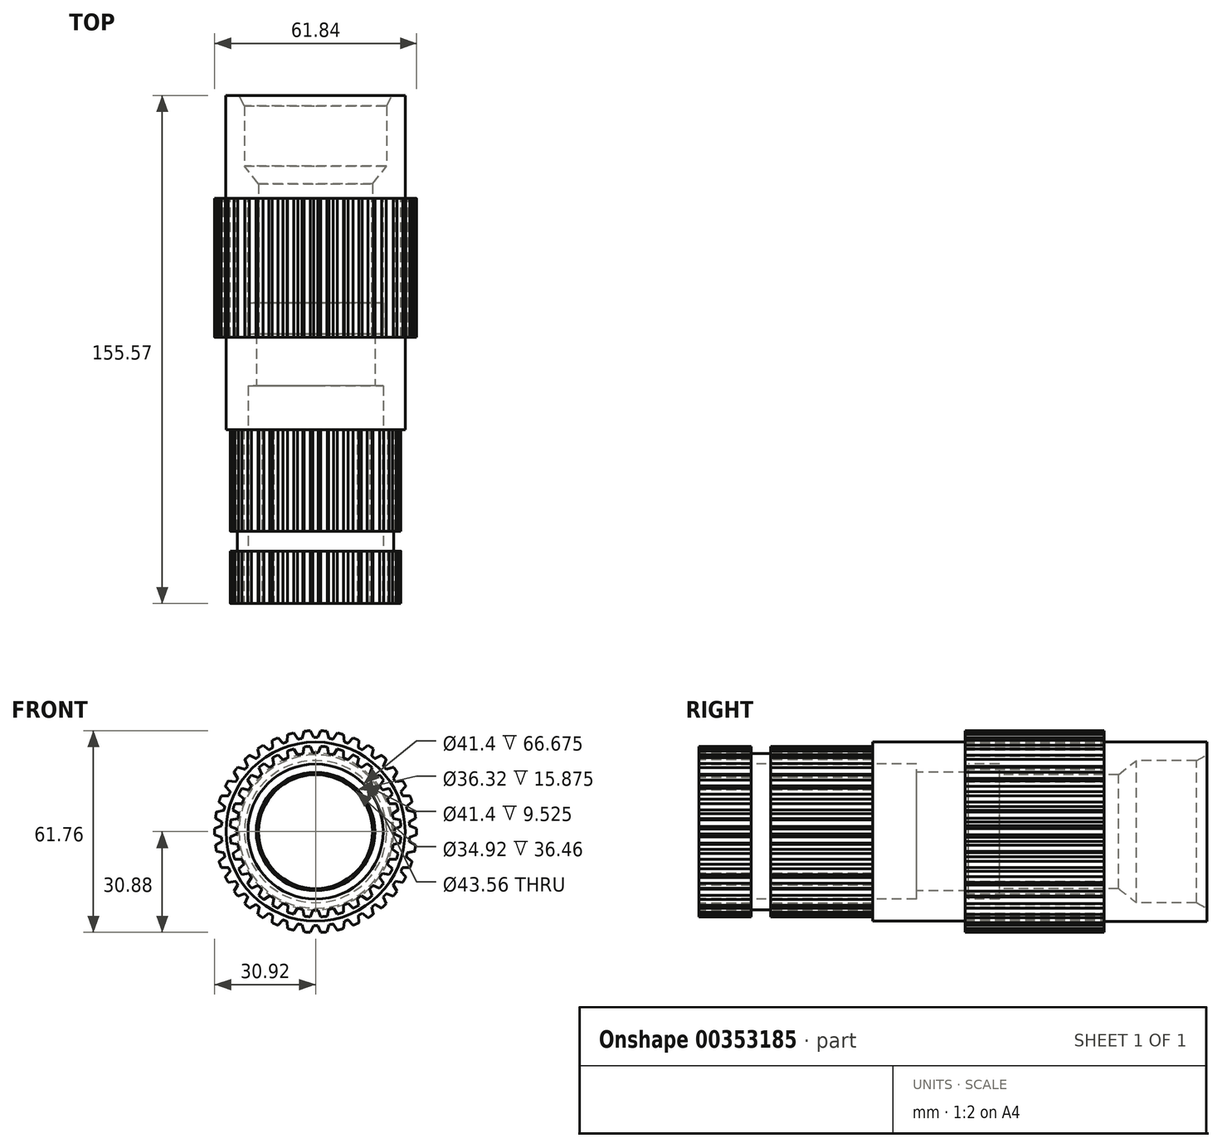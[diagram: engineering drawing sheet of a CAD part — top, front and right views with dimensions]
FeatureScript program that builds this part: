
annotation { "Feature Type Name" : "Feature", "Feature Type Description" : "" }
export const myFeature = defineFeature(function(context is Context, id is Id, definition is map)
    precondition{}
    {
        {
            var Q0;
            Q0=qCreatedBy(makeId("Right.planeOp"),FACE);
            var sketch = newSketch(context, id + "F0", { "sketchPlane" : qUnion([Q0])});
            skLineSegment(sketch, "E0", {"start": v(0, 0) * mm, "end": v(83.81, 0) * mm});
            skLineSegment(sketch, "E1", {"start": v(83.81, 0) * mm, "end": v(83.81, 27.5) * mm});
            skLineSegment(sketch, "E2", {"start": v(83.81, 27.5) * mm, "end": v(52.32, 27.5) * mm});
            skLineSegment(sketch, "E3", {"start": v(52.32, 27.5) * mm, "end": v(52.32, 30.92) * mm});
            skLineSegment(sketch, "E4", {"start": v(52.32, 30.92) * mm, "end": v(9.77, 30.92) * mm});
            skLineSegment(sketch, "E5", {"start": v(9.77, 30.92) * mm, "end": v(9.77, 27.43) * mm});
            skLineSegment(sketch, "E6", {"start": v(9.77, 27.43) * mm, "end": v(-18.53, 27.43) * mm});
            skLineSegment(sketch, "E7", {"start": v(-18.53, 27.43) * mm, "end": v(-18.53, 26.16) * mm});
            skLineSegment(sketch, "E8", {"start": v(-18.53, 26.16) * mm, "end": v(-49.7, 26.16) * mm});
            skLineSegment(sketch, "E9", {"start": v(-49.7, 26.16) * mm, "end": v(-49.7, 23.96) * mm});
            skLineSegment(sketch, "E10", {"start": v(-49.7, 23.96) * mm, "end": v(-55.71, 23.96) * mm});
            skLineSegment(sketch, "E11", {"start": v(-55.71, 23.96) * mm, "end": v(-55.71, 26.16) * mm});
            skLineSegment(sketch, "E12", {"start": v(-55.71, 26.16) * mm, "end": v(-71.76, 26.16) * mm});
            skLineSegment(sketch, "E13", {"start": v(-71.76, 26.16) * mm, "end": v(-71.76, 0) * mm});
            skLineSegment(sketch, "E14", {"start": v(-71.76, 0) * mm, "end": v(0, 0) * mm});
            skLineSegment(sketch, "E15", {"start": v(83.81, 23.5) * mm, "end": v(80.64, 21.78) * mm});
            skLineSegment(sketch, "E16", {"start": v(80.64, 21.78) * mm, "end": v(62.22, 21.78) * mm});
            skLineSegment(sketch, "E17", {"start": v(62.22, 21.78) * mm, "end": v(56.77, 17.46) * mm});
            skLineSegment(sketch, "E18", {"start": v(56.77, 17.46) * mm, "end": v(20.31, 17.46) * mm});
            skLineSegment(sketch, "E19", {"start": v(20.31, 17.46) * mm, "end": v(20.31, 20.7) * mm});
            skLineSegment(sketch, "E20", {"start": v(20.31, 20.7) * mm, "end": v(10.79, 20.7) * mm});
            skLineSegment(sketch, "E21", {"start": v(10.79, 20.7) * mm, "end": v(10.79, 18.16) * mm});
            skLineSegment(sketch, "E22", {"start": v(10.79, 18.16) * mm, "end": v(-5.09, 18.16) * mm});
            skLineSegment(sketch, "E23", {"start": v(-5.09, 18.16) * mm, "end": v(-5.09, 20.7) * mm});
            skLineSegment(sketch, "E24", {"start": v(-5.09, 20.7) * mm, "end": v(-71.76, 20.7) * mm});
            skSolve(sketch);
        }
        {
            var Q0;
            {var subQ4=sQuery(id+"F0.wireOp",EDGE,"E2");Q0=makeQuery(id+"F0.imprint","IMPRINT",FACE,{"disambiguationData":[TD([[makeQuery(id+"F0.imprint","IMPRINT",EDGE,{"derivedFrom":subQ4}),1.0]])]});}
            var Q1;
            Q1=sQuery(id+"F0.wireOp",EDGE,"E0");
            revolve(context, id + "F1", {"entities" : qUnion([Q0]), "axis" : qUnion([Q1]), "revolveType" : RevolveType.FULL});
        }
        {
            var Q0;
            Q0=makeQuery(id+"F1.opRevolve","SWEPT_FACE",FACE,{"disambiguationData":[OSD([sQuery(id+"F0.wireOp",EDGE,"E3")])]});
            var sketch = newSketch(context, id + "F2", { "sketchPlane" : qUnion([Q0])});
            skLineSegment(sketch, "E25", {"start": v(0, 0) * mm, "end": v(0, 43.98) * mm});
            skLineSegment(sketch, "E26.0", {"start": v(0.64, 0) * mm, "end": v(0.64, 43.98) * mm});
            skLineSegment(sketch, "E27.0", {"start": v(1.57, 0) * mm, "end": v(1.57, 43.98) * mm});
            skCircle(sketch, "E28", {"center": v(0, 0) * mm, "radius": 28.83 * mm});
            skLineSegment(sketch, "E29", {"start": v(1.57, 30.88) * mm, "end": v(0.64, 28.82) * mm});
            skLineSegment(sketch, "E30.MirrorCS", {"start": v(-1.57, 30.88) * mm, "end": v(-0.63, 28.82) * mm});
            skLineSegment(sketch, "E31.1.0", {"start": v(-6.64, 30.2) * mm, "end": v(-5.37, 28.32) * mm});
            skLineSegment(sketch, "E31.1.1", {"start": v(-3.53, 30.72) * mm, "end": v(-4.12, 28.53) * mm});
            skLineSegment(sketch, "E31.2.0", {"start": v(-11.52, 28.7) * mm, "end": v(-9.96, 27.05) * mm});
            skLineSegment(sketch, "E31.2.1", {"start": v(-8.54, 29.72) * mm, "end": v(-8.76, 27.47) * mm});
            skLineSegment(sketch, "E31.3.0", {"start": v(-16.08, 26.41) * mm, "end": v(-14.28, 25.05) * mm});
            skLineSegment(sketch, "E31.3.1", {"start": v(-13.31, 27.91) * mm, "end": v(-13.16, 25.65) * mm});
            skLineSegment(sketch, "E31.4.0", {"start": v(-20.21, 23.4) * mm, "end": v(-18.2, 22.35) * mm});
            skLineSegment(sketch, "E31.4.1", {"start": v(-17.73, 25.34) * mm, "end": v(-17.2, 23.13) * mm});
            skLineSegment(sketch, "E31.5.0", {"start": v(-23.79, 19.76) * mm, "end": v(-21.64, 19.05) * mm});
            skLineSegment(sketch, "E31.5.1", {"start": v(-21.66, 22.08) * mm, "end": v(-20.77, 19.99) * mm});
            skLineSegment(sketch, "E31.6.0", {"start": v(-26.72, 15.57) * mm, "end": v(-24.48, 15.23) * mm});
            skLineSegment(sketch, "E31.6.1", {"start": v(-25, 18.21) * mm, "end": v(-23.78, 16.3) * mm});
            skLineSegment(sketch, "E31.7.0", {"start": v(-28.92, 10.96) * mm, "end": v(-26.65, 11) * mm});
            skLineSegment(sketch, "E31.7.1", {"start": v(-27.65, 13.85) * mm, "end": v(-26.14, 12.16) * mm});
            skLineSegment(sketch, "E31.8.0", {"start": v(-30.33, 6.06) * mm, "end": v(-28.1, 6.46) * mm});
            skLineSegment(sketch, "E31.8.1", {"start": v(-29.55, 9.1) * mm, "end": v(-27.78, 7.7) * mm});
            skLineSegment(sketch, "E31.9.0", {"start": v(-30.9, 0.98) * mm, "end": v(-28.78, 1.75) * mm});
            skLineSegment(sketch, "E31.9.1", {"start": v(-30.65, 4.12) * mm, "end": v(-28.67, 3.01) * mm});
            skLineSegment(sketch, "E31.10.0", {"start": v(-30.65, -4.12) * mm, "end": v(-28.67, -3.01) * mm});
            skLineSegment(sketch, "E31.10.1", {"start": v(-30.9, -0.98) * mm, "end": v(-28.78, -1.75) * mm});
            skLineSegment(sketch, "E31.11.0", {"start": v(-29.55, -9.1) * mm, "end": v(-27.78, -7.7) * mm});
            skLineSegment(sketch, "E31.11.1", {"start": v(-30.33, -6.06) * mm, "end": v(-28.1, -6.46) * mm});
            skLineSegment(sketch, "E31.12.0", {"start": v(-27.65, -13.85) * mm, "end": v(-26.14, -12.16) * mm});
            skLineSegment(sketch, "E31.12.1", {"start": v(-28.92, -10.96) * mm, "end": v(-26.65, -11) * mm});
            skLineSegment(sketch, "E31.13.0", {"start": v(-25, -18.21) * mm, "end": v(-23.78, -16.3) * mm});
            skLineSegment(sketch, "E31.13.1", {"start": v(-26.72, -15.57) * mm, "end": v(-24.48, -15.23) * mm});
            skLineSegment(sketch, "E31.14.0", {"start": v(-21.66, -22.08) * mm, "end": v(-20.77, -19.99) * mm});
            skLineSegment(sketch, "E31.14.1", {"start": v(-23.79, -19.76) * mm, "end": v(-21.64, -19.05) * mm});
            skLineSegment(sketch, "E31.15.0", {"start": v(-17.73, -25.34) * mm, "end": v(-17.2, -23.13) * mm});
            skLineSegment(sketch, "E31.15.1", {"start": v(-20.21, -23.4) * mm, "end": v(-18.2, -22.35) * mm});
            skLineSegment(sketch, "E31.16.0", {"start": v(-13.31, -27.91) * mm, "end": v(-13.16, -25.65) * mm});
            skLineSegment(sketch, "E31.16.1", {"start": v(-16.08, -26.41) * mm, "end": v(-14.28, -25.05) * mm});
            skLineSegment(sketch, "E31.17.0", {"start": v(-8.54, -29.72) * mm, "end": v(-8.76, -27.47) * mm});
            skLineSegment(sketch, "E31.17.1", {"start": v(-11.52, -28.7) * mm, "end": v(-9.96, -27.05) * mm});
            skLineSegment(sketch, "E31.18.0", {"start": v(-3.53, -30.72) * mm, "end": v(-4.12, -28.53) * mm});
            skLineSegment(sketch, "E31.18.1", {"start": v(-6.64, -30.2) * mm, "end": v(-5.37, -28.32) * mm});
            skLineSegment(sketch, "E31.19.0", {"start": v(1.57, -30.88) * mm, "end": v(0.63, -28.82) * mm});
            skLineSegment(sketch, "E31.19.1", {"start": v(-1.57, -30.88) * mm, "end": v(-0.64, -28.82) * mm});
            skLineSegment(sketch, "E31.20.0", {"start": v(6.64, -30.2) * mm, "end": v(5.37, -28.32) * mm});
            skLineSegment(sketch, "E31.20.1", {"start": v(3.53, -30.72) * mm, "end": v(4.12, -28.53) * mm});
            skLineSegment(sketch, "E31.21.0", {"start": v(11.52, -28.7) * mm, "end": v(9.96, -27.05) * mm});
            skLineSegment(sketch, "E31.21.1", {"start": v(8.54, -29.72) * mm, "end": v(8.76, -27.47) * mm});
            skLineSegment(sketch, "E31.22.0", {"start": v(16.08, -26.41) * mm, "end": v(14.28, -25.05) * mm});
            skLineSegment(sketch, "E31.22.1", {"start": v(13.31, -27.91) * mm, "end": v(13.16, -25.65) * mm});
            skLineSegment(sketch, "E31.23.0", {"start": v(20.21, -23.4) * mm, "end": v(18.2, -22.35) * mm});
            skLineSegment(sketch, "E31.23.1", {"start": v(17.73, -25.34) * mm, "end": v(17.2, -23.13) * mm});
            skLineSegment(sketch, "E31.24.0", {"start": v(23.79, -19.76) * mm, "end": v(21.64, -19.05) * mm});
            skLineSegment(sketch, "E31.24.1", {"start": v(21.66, -22.08) * mm, "end": v(20.77, -19.99) * mm});
            skLineSegment(sketch, "E31.25.0", {"start": v(26.72, -15.57) * mm, "end": v(24.48, -15.23) * mm});
            skLineSegment(sketch, "E31.25.1", {"start": v(25, -18.21) * mm, "end": v(23.78, -16.3) * mm});
            skLineSegment(sketch, "E31.26.0", {"start": v(28.92, -10.96) * mm, "end": v(26.65, -11) * mm});
            skLineSegment(sketch, "E31.26.1", {"start": v(27.65, -13.85) * mm, "end": v(26.14, -12.16) * mm});
            skLineSegment(sketch, "E31.27.0", {"start": v(30.33, -6.06) * mm, "end": v(28.1, -6.46) * mm});
            skLineSegment(sketch, "E31.27.1", {"start": v(29.55, -9.1) * mm, "end": v(27.78, -7.7) * mm});
            skLineSegment(sketch, "E31.28.0", {"start": v(30.9, -0.98) * mm, "end": v(28.78, -1.75) * mm});
            skLineSegment(sketch, "E31.28.1", {"start": v(30.65, -4.12) * mm, "end": v(28.67, -3.01) * mm});
            skLineSegment(sketch, "E31.29.0", {"start": v(30.65, 4.12) * mm, "end": v(28.67, 3.01) * mm});
            skLineSegment(sketch, "E31.29.1", {"start": v(30.9, 0.98) * mm, "end": v(28.78, 1.75) * mm});
            skLineSegment(sketch, "E31.30.0", {"start": v(29.55, 9.1) * mm, "end": v(27.78, 7.7) * mm});
            skLineSegment(sketch, "E31.30.1", {"start": v(30.33, 6.06) * mm, "end": v(28.1, 6.46) * mm});
            skLineSegment(sketch, "E31.31.0", {"start": v(27.65, 13.85) * mm, "end": v(26.14, 12.16) * mm});
            skLineSegment(sketch, "E31.31.1", {"start": v(28.92, 10.96) * mm, "end": v(26.65, 11) * mm});
            skLineSegment(sketch, "E31.32.0", {"start": v(25, 18.21) * mm, "end": v(23.78, 16.3) * mm});
            skLineSegment(sketch, "E31.32.1", {"start": v(26.72, 15.57) * mm, "end": v(24.48, 15.23) * mm});
            skLineSegment(sketch, "E31.33.0", {"start": v(21.66, 22.08) * mm, "end": v(20.77, 19.99) * mm});
            skLineSegment(sketch, "E31.33.1", {"start": v(23.79, 19.76) * mm, "end": v(21.64, 19.05) * mm});
            skLineSegment(sketch, "E31.34.0", {"start": v(17.73, 25.34) * mm, "end": v(17.2, 23.13) * mm});
            skLineSegment(sketch, "E31.34.1", {"start": v(20.21, 23.4) * mm, "end": v(18.2, 22.35) * mm});
            skLineSegment(sketch, "E31.35.0", {"start": v(13.31, 27.91) * mm, "end": v(13.16, 25.65) * mm});
            skLineSegment(sketch, "E31.35.1", {"start": v(16.08, 26.41) * mm, "end": v(14.28, 25.05) * mm});
            skLineSegment(sketch, "E31.36.0", {"start": v(8.54, 29.72) * mm, "end": v(8.76, 27.47) * mm});
            skLineSegment(sketch, "E31.36.1", {"start": v(11.52, 28.7) * mm, "end": v(9.96, 27.05) * mm});
            skLineSegment(sketch, "E31.37.0", {"start": v(3.53, 30.72) * mm, "end": v(4.12, 28.53) * mm});
            skLineSegment(sketch, "E31.37.1", {"start": v(6.64, 30.2) * mm, "end": v(5.37, 28.32) * mm});
            skSolve(sketch);
        }
        {
            var Q0;
            {var subQ5=sQuery(id+"F2.wireOp",EDGE,"E30.MirrorCS");Q0=makeQuery(id+"F2.imprint","IMPRINT",FACE,{"disambiguationData":[TD([[makeQuery(id+"F2.imprint","IMPRINT",EDGE,{"derivedFrom":subQ5}),1.0]])]});}
            var Q1;
            {var subQ0=sQuery(id+"F2.wireOp",EDGE,"E28");var subQ1=sQuery(id+"F2.wireOp",EDGE,"E25");var subQ2=makeQuery(id+"F2.imprint","INTERSECT",VERTEX,{"derivedFrom":[subQ1,subQ0]});Q1=makeQuery(id+"F2.imprint","IMPRINT",FACE,{"disambiguationData":[TD([[makeQuery(id+"F2.imprint","IMPRINT",EDGE,{"disambiguationData":[TD([[subQ2,-1.0]])],"derivedFrom":subQ1}),-1.0]])]});}
            var Q2;
            {var subQ0=sQuery(id+"F2.wireOp",EDGE,"E29");Q2=makeQuery(id+"F2.imprint","IMPRINT",FACE,{"disambiguationData":[TD([[makeQuery(id+"F2.imprint","IMPRINT",EDGE,{"derivedFrom":subQ0}),-1.0]])]});}
            var Q3;
            {var subQ0=sQuery(id+"F2.wireOp",EDGE,"E31.37.0");Q3=makeQuery(id+"F2.imprint","IMPRINT",FACE,{"disambiguationData":[TD([[makeQuery(id+"F2.imprint","IMPRINT",EDGE,{"derivedFrom":subQ0}),1.0]])]});}
            var Q4;
            {var subQ0=sQuery(id+"F2.wireOp",EDGE,"E31.36.0");Q4=makeQuery(id+"F2.imprint","IMPRINT",FACE,{"disambiguationData":[TD([[makeQuery(id+"F2.imprint","IMPRINT",EDGE,{"derivedFrom":subQ0}),1.0]])]});}
            var Q5;
            {var subQ0=sQuery(id+"F2.wireOp",EDGE,"E31.35.0");Q5=makeQuery(id+"F2.imprint","IMPRINT",FACE,{"disambiguationData":[TD([[makeQuery(id+"F2.imprint","IMPRINT",EDGE,{"derivedFrom":subQ0}),1.0]])]});}
            var Q6;
            {var subQ0=sQuery(id+"F2.wireOp",EDGE,"E31.34.0");Q6=makeQuery(id+"F2.imprint","IMPRINT",FACE,{"disambiguationData":[TD([[makeQuery(id+"F2.imprint","IMPRINT",EDGE,{"derivedFrom":subQ0}),1.0]])]});}
            var Q7;
            {var subQ0=sQuery(id+"F2.wireOp",EDGE,"E31.33.0");Q7=makeQuery(id+"F2.imprint","IMPRINT",FACE,{"disambiguationData":[TD([[makeQuery(id+"F2.imprint","IMPRINT",EDGE,{"derivedFrom":subQ0}),1.0]])]});}
            var Q8;
            {var subQ0=sQuery(id+"F2.wireOp",EDGE,"E31.32.0");Q8=makeQuery(id+"F2.imprint","IMPRINT",FACE,{"disambiguationData":[TD([[makeQuery(id+"F2.imprint","IMPRINT",EDGE,{"derivedFrom":subQ0}),1.0]])]});}
            var Q9;
            {var subQ0=sQuery(id+"F2.wireOp",EDGE,"E31.31.0");Q9=makeQuery(id+"F2.imprint","IMPRINT",FACE,{"disambiguationData":[TD([[makeQuery(id+"F2.imprint","IMPRINT",EDGE,{"derivedFrom":subQ0}),1.0]])]});}
            var Q10;
            {var subQ0=sQuery(id+"F2.wireOp",EDGE,"E31.30.0");Q10=makeQuery(id+"F2.imprint","IMPRINT",FACE,{"disambiguationData":[TD([[makeQuery(id+"F2.imprint","IMPRINT",EDGE,{"derivedFrom":subQ0}),1.0]])]});}
            var Q11;
            {var subQ0=sQuery(id+"F2.wireOp",EDGE,"E31.29.0");Q11=makeQuery(id+"F2.imprint","IMPRINT",FACE,{"disambiguationData":[TD([[makeQuery(id+"F2.imprint","IMPRINT",EDGE,{"derivedFrom":subQ0}),1.0]])]});}
            var Q12;
            {var subQ0=sQuery(id+"F2.wireOp",EDGE,"E31.28.0");Q12=makeQuery(id+"F2.imprint","IMPRINT",FACE,{"disambiguationData":[TD([[makeQuery(id+"F2.imprint","IMPRINT",EDGE,{"derivedFrom":subQ0}),1.0]])]});}
            var Q13;
            {var subQ0=sQuery(id+"F2.wireOp",EDGE,"E31.27.0");Q13=makeQuery(id+"F2.imprint","IMPRINT",FACE,{"disambiguationData":[TD([[makeQuery(id+"F2.imprint","IMPRINT",EDGE,{"derivedFrom":subQ0}),1.0]])]});}
            var Q14;
            {var subQ0=sQuery(id+"F2.wireOp",EDGE,"E31.26.0");Q14=makeQuery(id+"F2.imprint","IMPRINT",FACE,{"disambiguationData":[TD([[makeQuery(id+"F2.imprint","IMPRINT",EDGE,{"derivedFrom":subQ0}),1.0]])]});}
            var Q15;
            {var subQ0=sQuery(id+"F2.wireOp",EDGE,"E31.25.0");Q15=makeQuery(id+"F2.imprint","IMPRINT",FACE,{"disambiguationData":[TD([[makeQuery(id+"F2.imprint","IMPRINT",EDGE,{"derivedFrom":subQ0}),1.0]])]});}
            var Q16;
            {var subQ0=sQuery(id+"F2.wireOp",EDGE,"E31.24.0");Q16=makeQuery(id+"F2.imprint","IMPRINT",FACE,{"disambiguationData":[TD([[makeQuery(id+"F2.imprint","IMPRINT",EDGE,{"derivedFrom":subQ0}),1.0]])]});}
            var Q17;
            {var subQ0=sQuery(id+"F2.wireOp",EDGE,"E31.23.0");Q17=makeQuery(id+"F2.imprint","IMPRINT",FACE,{"disambiguationData":[TD([[makeQuery(id+"F2.imprint","IMPRINT",EDGE,{"derivedFrom":subQ0}),1.0]])]});}
            var Q18;
            {var subQ0=sQuery(id+"F2.wireOp",EDGE,"E31.22.0");Q18=makeQuery(id+"F2.imprint","IMPRINT",FACE,{"disambiguationData":[TD([[makeQuery(id+"F2.imprint","IMPRINT",EDGE,{"derivedFrom":subQ0}),1.0]])]});}
            var Q19;
            {var subQ0=sQuery(id+"F2.wireOp",EDGE,"E31.21.0");Q19=makeQuery(id+"F2.imprint","IMPRINT",FACE,{"disambiguationData":[TD([[makeQuery(id+"F2.imprint","IMPRINT",EDGE,{"derivedFrom":subQ0}),1.0]])]});}
            var Q20;
            {var subQ0=sQuery(id+"F2.wireOp",EDGE,"E31.20.0");Q20=makeQuery(id+"F2.imprint","IMPRINT",FACE,{"disambiguationData":[TD([[makeQuery(id+"F2.imprint","IMPRINT",EDGE,{"derivedFrom":subQ0}),1.0]])]});}
            var Q21;
            {var subQ0=sQuery(id+"F2.wireOp",EDGE,"E31.19.0");Q21=makeQuery(id+"F2.imprint","IMPRINT",FACE,{"disambiguationData":[TD([[makeQuery(id+"F2.imprint","IMPRINT",EDGE,{"derivedFrom":subQ0}),1.0]])]});}
            var Q22;
            {var subQ0=sQuery(id+"F2.wireOp",EDGE,"E31.18.0");Q22=makeQuery(id+"F2.imprint","IMPRINT",FACE,{"disambiguationData":[TD([[makeQuery(id+"F2.imprint","IMPRINT",EDGE,{"derivedFrom":subQ0}),1.0]])]});}
            var Q23;
            {var subQ0=sQuery(id+"F2.wireOp",EDGE,"E31.17.0");Q23=makeQuery(id+"F2.imprint","IMPRINT",FACE,{"disambiguationData":[TD([[makeQuery(id+"F2.imprint","IMPRINT",EDGE,{"derivedFrom":subQ0}),1.0]])]});}
            var Q24;
            {var subQ0=sQuery(id+"F2.wireOp",EDGE,"E31.16.0");Q24=makeQuery(id+"F2.imprint","IMPRINT",FACE,{"disambiguationData":[TD([[makeQuery(id+"F2.imprint","IMPRINT",EDGE,{"derivedFrom":subQ0}),1.0]])]});}
            var Q25;
            {var subQ0=sQuery(id+"F2.wireOp",EDGE,"E31.15.0");Q25=makeQuery(id+"F2.imprint","IMPRINT",FACE,{"disambiguationData":[TD([[makeQuery(id+"F2.imprint","IMPRINT",EDGE,{"derivedFrom":subQ0}),1.0]])]});}
            var Q26;
            {var subQ0=sQuery(id+"F2.wireOp",EDGE,"E31.14.0");Q26=makeQuery(id+"F2.imprint","IMPRINT",FACE,{"disambiguationData":[TD([[makeQuery(id+"F2.imprint","IMPRINT",EDGE,{"derivedFrom":subQ0}),1.0]])]});}
            var Q27;
            {var subQ0=sQuery(id+"F2.wireOp",EDGE,"E31.13.0");Q27=makeQuery(id+"F2.imprint","IMPRINT",FACE,{"disambiguationData":[TD([[makeQuery(id+"F2.imprint","IMPRINT",EDGE,{"derivedFrom":subQ0}),1.0]])]});}
            var Q28;
            {var subQ0=sQuery(id+"F2.wireOp",EDGE,"E31.12.0");Q28=makeQuery(id+"F2.imprint","IMPRINT",FACE,{"disambiguationData":[TD([[makeQuery(id+"F2.imprint","IMPRINT",EDGE,{"derivedFrom":subQ0}),1.0]])]});}
            var Q29;
            {var subQ0=sQuery(id+"F2.wireOp",EDGE,"E31.11.0");Q29=makeQuery(id+"F2.imprint","IMPRINT",FACE,{"disambiguationData":[TD([[makeQuery(id+"F2.imprint","IMPRINT",EDGE,{"derivedFrom":subQ0}),1.0]])]});}
            var Q30;
            {var subQ0=sQuery(id+"F2.wireOp",EDGE,"E31.10.0");Q30=makeQuery(id+"F2.imprint","IMPRINT",FACE,{"disambiguationData":[TD([[makeQuery(id+"F2.imprint","IMPRINT",EDGE,{"derivedFrom":subQ0}),1.0]])]});}
            var Q31;
            {var subQ0=sQuery(id+"F2.wireOp",EDGE,"E31.9.0");Q31=makeQuery(id+"F2.imprint","IMPRINT",FACE,{"disambiguationData":[TD([[makeQuery(id+"F2.imprint","IMPRINT",EDGE,{"derivedFrom":subQ0}),1.0]])]});}
            var Q32;
            {var subQ0=sQuery(id+"F2.wireOp",EDGE,"E31.8.0");Q32=makeQuery(id+"F2.imprint","IMPRINT",FACE,{"disambiguationData":[TD([[makeQuery(id+"F2.imprint","IMPRINT",EDGE,{"derivedFrom":subQ0}),1.0]])]});}
            var Q33;
            {var subQ0=sQuery(id+"F2.wireOp",EDGE,"E31.7.0");Q33=makeQuery(id+"F2.imprint","IMPRINT",FACE,{"disambiguationData":[TD([[makeQuery(id+"F2.imprint","IMPRINT",EDGE,{"derivedFrom":subQ0}),1.0]])]});}
            var Q34;
            {var subQ0=sQuery(id+"F2.wireOp",EDGE,"E31.6.0");Q34=makeQuery(id+"F2.imprint","IMPRINT",FACE,{"disambiguationData":[TD([[makeQuery(id+"F2.imprint","IMPRINT",EDGE,{"derivedFrom":subQ0}),1.0]])]});}
            var Q35;
            {var subQ0=sQuery(id+"F2.wireOp",EDGE,"E31.5.0");Q35=makeQuery(id+"F2.imprint","IMPRINT",FACE,{"disambiguationData":[TD([[makeQuery(id+"F2.imprint","IMPRINT",EDGE,{"derivedFrom":subQ0}),1.0]])]});}
            var Q36;
            {var subQ0=sQuery(id+"F2.wireOp",EDGE,"E31.4.0");Q36=makeQuery(id+"F2.imprint","IMPRINT",FACE,{"disambiguationData":[TD([[makeQuery(id+"F2.imprint","IMPRINT",EDGE,{"derivedFrom":subQ0}),1.0]])]});}
            var Q37;
            {var subQ0=sQuery(id+"F2.wireOp",EDGE,"E31.3.0");Q37=makeQuery(id+"F2.imprint","IMPRINT",FACE,{"disambiguationData":[TD([[makeQuery(id+"F2.imprint","IMPRINT",EDGE,{"derivedFrom":subQ0}),1.0]])]});}
            var Q38;
            {var subQ0=sQuery(id+"F2.wireOp",EDGE,"E31.2.0");Q38=makeQuery(id+"F2.imprint","IMPRINT",FACE,{"disambiguationData":[TD([[makeQuery(id+"F2.imprint","IMPRINT",EDGE,{"derivedFrom":subQ0}),1.0]])]});}
            var Q39;
            {var subQ0=sQuery(id+"F2.wireOp",EDGE,"E31.1.0");Q39=makeQuery(id+"F2.imprint","IMPRINT",FACE,{"disambiguationData":[TD([[makeQuery(id+"F2.imprint","IMPRINT",EDGE,{"derivedFrom":subQ0}),1.0]])]});}
            extrude(context, id + "F3", {"entities" : qUnion([Q0, Q1, Q2, Q3, Q4, Q5, Q6, Q7, Q8, Q9, Q10, Q11, Q12, Q13, Q14, Q15, Q16, Q17, Q18, Q19, Q20, Q21, Q22, Q23, Q24, Q25, Q26, Q27, Q28, Q29, Q30, Q31, Q32, Q33, Q34, Q35, Q36, Q37, Q38, Q39]), "operationType" : NewBodyOperationType.REMOVE, "endBound" : BoundingType.UP_TO_NEXT, "oppositeDirection" : true, "depth" : 25.4 * mm});
        }
        {
            var Q0;
            Q0=makeQuery(id+"F1.opRevolve","SWEPT_FACE",FACE,{"disambiguationData":[OSD([sQuery(id+"F0.wireOp",EDGE,"E13")])]});
            var sketch = newSketch(context, id + "F4", { "sketchPlane" : qUnion([Q0])});
            skCircle(sketch, "E32", {"center": v(0, 0) * mm, "radius": 24.13 * mm});
            skLineSegment(sketch, "E33", {"start": v(0, 0) * mm, "end": v(0, 32.18) * mm});
            skLineSegment(sketch, "E34.0", {"start": v(0.79, 0) * mm, "end": v(0.79, 32.18) * mm});
            skLineSegment(sketch, "E35.0", {"start": v(1.57, 0) * mm, "end": v(1.57, 32.18) * mm});
            skLineSegment(sketch, "E36", {"start": v(1.57, 26.11) * mm, "end": v(0.79, 24.12) * mm});
            skLineSegment(sketch, "E37.MirrorCS", {"start": v(-1.57, 26.11) * mm, "end": v(-0.79, 24.12) * mm});
            skLineSegment(sketch, "E38.1.0", {"start": v(-6.64, 25.3) * mm, "end": v(-5.48, 23.5) * mm});
            skLineSegment(sketch, "E38.1.1", {"start": v(-3.55, 25.92) * mm, "end": v(-3.93, 23.8) * mm});
            skLineSegment(sketch, "E38.2.0", {"start": v(-11.45, 23.52) * mm, "end": v(-9.96, 21.98) * mm});
            skLineSegment(sketch, "E38.2.1", {"start": v(-8.54, 24.73) * mm, "end": v(-8.5, 22.58) * mm});
            skLineSegment(sketch, "E38.3.0", {"start": v(-15.82, 20.84) * mm, "end": v(-14.05, 19.62) * mm});
            skLineSegment(sketch, "E38.3.1", {"start": v(-13.2, 22.59) * mm, "end": v(-12.74, 20.5) * mm});
            skLineSegment(sketch, "E38.4.0", {"start": v(-19.58, 17.35) * mm, "end": v(-17.61, 16.5) * mm});
            skLineSegment(sketch, "E38.4.1", {"start": v(-17.35, 19.58) * mm, "end": v(-16.5, 17.61) * mm});
            skLineSegment(sketch, "E38.5.0", {"start": v(-22.59, 13.2) * mm, "end": v(-20.5, 12.74) * mm});
            skLineSegment(sketch, "E38.5.1", {"start": v(-20.84, 15.82) * mm, "end": v(-19.62, 14.05) * mm});
            skLineSegment(sketch, "E38.6.0", {"start": v(-24.73, 8.54) * mm, "end": v(-22.58, 8.5) * mm});
            skLineSegment(sketch, "E38.6.1", {"start": v(-23.52, 11.45) * mm, "end": v(-21.98, 9.96) * mm});
            skLineSegment(sketch, "E38.7.0", {"start": v(-25.92, 3.55) * mm, "end": v(-23.8, 3.93) * mm});
            skLineSegment(sketch, "E38.7.1", {"start": v(-25.3, 6.64) * mm, "end": v(-23.5, 5.48) * mm});
            skLineSegment(sketch, "E38.8.0", {"start": v(-26.11, -1.57) * mm, "end": v(-24.12, -0.79) * mm});
            skLineSegment(sketch, "E38.8.1", {"start": v(-26.11, 1.57) * mm, "end": v(-24.12, 0.79) * mm});
            skLineSegment(sketch, "E38.9.0", {"start": v(-25.3, -6.64) * mm, "end": v(-23.5, -5.48) * mm});
            skLineSegment(sketch, "E38.9.1", {"start": v(-25.92, -3.55) * mm, "end": v(-23.8, -3.93) * mm});
            skLineSegment(sketch, "E38.10.0", {"start": v(-23.52, -11.45) * mm, "end": v(-21.98, -9.96) * mm});
            skLineSegment(sketch, "E38.10.1", {"start": v(-24.73, -8.54) * mm, "end": v(-22.58, -8.5) * mm});
            skLineSegment(sketch, "E38.11.0", {"start": v(-20.84, -15.82) * mm, "end": v(-19.62, -14.05) * mm});
            skLineSegment(sketch, "E38.11.1", {"start": v(-22.59, -13.2) * mm, "end": v(-20.5, -12.74) * mm});
            skLineSegment(sketch, "E38.12.0", {"start": v(-17.35, -19.58) * mm, "end": v(-16.5, -17.61) * mm});
            skLineSegment(sketch, "E38.12.1", {"start": v(-19.58, -17.35) * mm, "end": v(-17.61, -16.5) * mm});
            skLineSegment(sketch, "E38.13.0", {"start": v(-13.2, -22.59) * mm, "end": v(-12.74, -20.5) * mm});
            skLineSegment(sketch, "E38.13.1", {"start": v(-15.82, -20.84) * mm, "end": v(-14.05, -19.62) * mm});
            skLineSegment(sketch, "E38.14.0", {"start": v(-8.54, -24.73) * mm, "end": v(-8.5, -22.58) * mm});
            skLineSegment(sketch, "E38.14.1", {"start": v(-11.45, -23.52) * mm, "end": v(-9.96, -21.98) * mm});
            skLineSegment(sketch, "E38.15.0", {"start": v(-3.55, -25.92) * mm, "end": v(-3.93, -23.8) * mm});
            skLineSegment(sketch, "E38.15.1", {"start": v(-6.64, -25.3) * mm, "end": v(-5.48, -23.5) * mm});
            skLineSegment(sketch, "E38.16.0", {"start": v(1.57, -26.11) * mm, "end": v(0.79, -24.12) * mm});
            skLineSegment(sketch, "E38.16.1", {"start": v(-1.57, -26.11) * mm, "end": v(-0.79, -24.12) * mm});
            skLineSegment(sketch, "E38.17.0", {"start": v(6.64, -25.3) * mm, "end": v(5.48, -23.5) * mm});
            skLineSegment(sketch, "E38.17.1", {"start": v(3.55, -25.92) * mm, "end": v(3.93, -23.8) * mm});
            skLineSegment(sketch, "E38.18.0", {"start": v(11.45, -23.52) * mm, "end": v(9.96, -21.98) * mm});
            skLineSegment(sketch, "E38.18.1", {"start": v(8.54, -24.73) * mm, "end": v(8.5, -22.58) * mm});
            skLineSegment(sketch, "E38.19.0", {"start": v(15.82, -20.84) * mm, "end": v(14.05, -19.62) * mm});
            skLineSegment(sketch, "E38.19.1", {"start": v(13.2, -22.59) * mm, "end": v(12.74, -20.5) * mm});
            skLineSegment(sketch, "E38.20.0", {"start": v(19.58, -17.35) * mm, "end": v(17.61, -16.5) * mm});
            skLineSegment(sketch, "E38.20.1", {"start": v(17.35, -19.58) * mm, "end": v(16.5, -17.61) * mm});
            skLineSegment(sketch, "E38.21.0", {"start": v(22.59, -13.2) * mm, "end": v(20.5, -12.74) * mm});
            skLineSegment(sketch, "E38.21.1", {"start": v(20.84, -15.82) * mm, "end": v(19.62, -14.05) * mm});
            skLineSegment(sketch, "E38.22.0", {"start": v(24.73, -8.54) * mm, "end": v(22.58, -8.5) * mm});
            skLineSegment(sketch, "E38.22.1", {"start": v(23.52, -11.45) * mm, "end": v(21.98, -9.96) * mm});
            skLineSegment(sketch, "E38.23.0", {"start": v(25.92, -3.55) * mm, "end": v(23.8, -3.93) * mm});
            skLineSegment(sketch, "E38.23.1", {"start": v(25.3, -6.64) * mm, "end": v(23.5, -5.48) * mm});
            skLineSegment(sketch, "E38.24.0", {"start": v(26.11, 1.57) * mm, "end": v(24.12, 0.79) * mm});
            skLineSegment(sketch, "E38.24.1", {"start": v(26.11, -1.57) * mm, "end": v(24.12, -0.79) * mm});
            skLineSegment(sketch, "E38.25.0", {"start": v(25.3, 6.64) * mm, "end": v(23.5, 5.48) * mm});
            skLineSegment(sketch, "E38.25.1", {"start": v(25.92, 3.55) * mm, "end": v(23.8, 3.93) * mm});
            skLineSegment(sketch, "E38.26.0", {"start": v(23.52, 11.45) * mm, "end": v(21.98, 9.96) * mm});
            skLineSegment(sketch, "E38.26.1", {"start": v(24.73, 8.54) * mm, "end": v(22.58, 8.5) * mm});
            skLineSegment(sketch, "E38.27.0", {"start": v(20.84, 15.82) * mm, "end": v(19.62, 14.05) * mm});
            skLineSegment(sketch, "E38.27.1", {"start": v(22.59, 13.2) * mm, "end": v(20.5, 12.74) * mm});
            skLineSegment(sketch, "E38.28.0", {"start": v(17.35, 19.58) * mm, "end": v(16.5, 17.61) * mm});
            skLineSegment(sketch, "E38.28.1", {"start": v(19.58, 17.35) * mm, "end": v(17.61, 16.5) * mm});
            skLineSegment(sketch, "E38.29.0", {"start": v(13.2, 22.59) * mm, "end": v(12.74, 20.5) * mm});
            skLineSegment(sketch, "E38.29.1", {"start": v(15.82, 20.84) * mm, "end": v(14.05, 19.62) * mm});
            skLineSegment(sketch, "E38.30.0", {"start": v(8.54, 24.73) * mm, "end": v(8.5, 22.58) * mm});
            skLineSegment(sketch, "E38.30.1", {"start": v(11.45, 23.52) * mm, "end": v(9.96, 21.98) * mm});
            skLineSegment(sketch, "E38.31.0", {"start": v(3.55, 25.92) * mm, "end": v(3.93, 23.8) * mm});
            skLineSegment(sketch, "E38.31.1", {"start": v(6.64, 25.3) * mm, "end": v(5.48, 23.5) * mm});
            skSolve(sketch);
        }
        {
            var Q0;
            {var subQ0=sQuery(id+"F4.wireOp",EDGE,"E37.MirrorCS");Q0=makeQuery(id+"F4.imprint","IMPRINT",FACE,{"disambiguationData":[TD([[makeQuery(id+"F4.imprint","IMPRINT",EDGE,{"derivedFrom":subQ0}),1.0]])]});}
            var Q1;
            {var subQ1=sQuery(id+"F4.wireOp",EDGE,"E32");var subQ3=sQuery(id+"F4.wireOp",EDGE,"E33");var subQ4=makeQuery(id+"F4.imprint","INTERSECT",VERTEX,{"derivedFrom":[subQ1,subQ3]});Q1=makeQuery(id+"F4.imprint","IMPRINT",FACE,{"disambiguationData":[TD([[makeQuery(id+"F4.imprint","IMPRINT",EDGE,{"disambiguationData":[TD([[subQ4,1.0]])],"derivedFrom":subQ1}),-1.0]])]});}
            var Q2;
            {var subQ0=sQuery(id+"F4.wireOp",EDGE,"E36");Q2=makeQuery(id+"F4.imprint","IMPRINT",FACE,{"disambiguationData":[TD([[makeQuery(id+"F4.imprint","IMPRINT",EDGE,{"derivedFrom":subQ0}),-1.0]])]});}
            var Q3;
            {var subQ0=sQuery(id+"F4.wireOp",EDGE,"E38.31.0");Q3=makeQuery(id+"F4.imprint","IMPRINT",FACE,{"disambiguationData":[TD([[makeQuery(id+"F4.imprint","IMPRINT",EDGE,{"derivedFrom":subQ0}),1.0]])]});}
            var Q4;
            {var subQ0=sQuery(id+"F4.wireOp",EDGE,"E38.30.0");Q4=makeQuery(id+"F4.imprint","IMPRINT",FACE,{"disambiguationData":[TD([[makeQuery(id+"F4.imprint","IMPRINT",EDGE,{"derivedFrom":subQ0}),1.0]])]});}
            var Q5;
            {var subQ0=sQuery(id+"F4.wireOp",EDGE,"E38.29.0");Q5=makeQuery(id+"F4.imprint","IMPRINT",FACE,{"disambiguationData":[TD([[makeQuery(id+"F4.imprint","IMPRINT",EDGE,{"derivedFrom":subQ0}),1.0]])]});}
            var Q6;
            {var subQ0=sQuery(id+"F4.wireOp",EDGE,"E38.28.0");Q6=makeQuery(id+"F4.imprint","IMPRINT",FACE,{"disambiguationData":[TD([[makeQuery(id+"F4.imprint","IMPRINT",EDGE,{"derivedFrom":subQ0}),1.0]])]});}
            var Q7;
            {var subQ0=sQuery(id+"F4.wireOp",EDGE,"E38.27.0");Q7=makeQuery(id+"F4.imprint","IMPRINT",FACE,{"disambiguationData":[TD([[makeQuery(id+"F4.imprint","IMPRINT",EDGE,{"derivedFrom":subQ0}),1.0]])]});}
            var Q8;
            {var subQ0=sQuery(id+"F4.wireOp",EDGE,"E38.26.0");Q8=makeQuery(id+"F4.imprint","IMPRINT",FACE,{"disambiguationData":[TD([[makeQuery(id+"F4.imprint","IMPRINT",EDGE,{"derivedFrom":subQ0}),1.0]])]});}
            var Q9;
            {var subQ0=sQuery(id+"F4.wireOp",EDGE,"E38.25.0");Q9=makeQuery(id+"F4.imprint","IMPRINT",FACE,{"disambiguationData":[TD([[makeQuery(id+"F4.imprint","IMPRINT",EDGE,{"derivedFrom":subQ0}),1.0]])]});}
            var Q10;
            {var subQ0=sQuery(id+"F4.wireOp",EDGE,"E38.24.0");Q10=makeQuery(id+"F4.imprint","IMPRINT",FACE,{"disambiguationData":[TD([[makeQuery(id+"F4.imprint","IMPRINT",EDGE,{"derivedFrom":subQ0}),1.0]])]});}
            var Q11;
            {var subQ0=sQuery(id+"F4.wireOp",EDGE,"E38.23.0");Q11=makeQuery(id+"F4.imprint","IMPRINT",FACE,{"disambiguationData":[TD([[makeQuery(id+"F4.imprint","IMPRINT",EDGE,{"derivedFrom":subQ0}),1.0]])]});}
            var Q12;
            {var subQ0=sQuery(id+"F4.wireOp",EDGE,"E38.22.0");Q12=makeQuery(id+"F4.imprint","IMPRINT",FACE,{"disambiguationData":[TD([[makeQuery(id+"F4.imprint","IMPRINT",EDGE,{"derivedFrom":subQ0}),1.0]])]});}
            var Q13;
            {var subQ0=sQuery(id+"F4.wireOp",EDGE,"E38.21.0");Q13=makeQuery(id+"F4.imprint","IMPRINT",FACE,{"disambiguationData":[TD([[makeQuery(id+"F4.imprint","IMPRINT",EDGE,{"derivedFrom":subQ0}),1.0]])]});}
            var Q14;
            {var subQ0=sQuery(id+"F4.wireOp",EDGE,"E38.20.0");Q14=makeQuery(id+"F4.imprint","IMPRINT",FACE,{"disambiguationData":[TD([[makeQuery(id+"F4.imprint","IMPRINT",EDGE,{"derivedFrom":subQ0}),1.0]])]});}
            var Q15;
            {var subQ0=sQuery(id+"F4.wireOp",EDGE,"E38.19.0");Q15=makeQuery(id+"F4.imprint","IMPRINT",FACE,{"disambiguationData":[TD([[makeQuery(id+"F4.imprint","IMPRINT",EDGE,{"derivedFrom":subQ0}),1.0]])]});}
            var Q16;
            {var subQ0=sQuery(id+"F4.wireOp",EDGE,"E38.18.0");Q16=makeQuery(id+"F4.imprint","IMPRINT",FACE,{"disambiguationData":[TD([[makeQuery(id+"F4.imprint","IMPRINT",EDGE,{"derivedFrom":subQ0}),1.0]])]});}
            var Q17;
            {var subQ0=sQuery(id+"F4.wireOp",EDGE,"E38.17.0");Q17=makeQuery(id+"F4.imprint","IMPRINT",FACE,{"disambiguationData":[TD([[makeQuery(id+"F4.imprint","IMPRINT",EDGE,{"derivedFrom":subQ0}),1.0]])]});}
            var Q18;
            {var subQ0=sQuery(id+"F4.wireOp",EDGE,"E38.16.0");Q18=makeQuery(id+"F4.imprint","IMPRINT",FACE,{"disambiguationData":[TD([[makeQuery(id+"F4.imprint","IMPRINT",EDGE,{"derivedFrom":subQ0}),1.0]])]});}
            var Q19;
            {var subQ0=sQuery(id+"F4.wireOp",EDGE,"E38.15.0");Q19=makeQuery(id+"F4.imprint","IMPRINT",FACE,{"disambiguationData":[TD([[makeQuery(id+"F4.imprint","IMPRINT",EDGE,{"derivedFrom":subQ0}),1.0]])]});}
            var Q20;
            {var subQ0=sQuery(id+"F4.wireOp",EDGE,"E38.14.0");Q20=makeQuery(id+"F4.imprint","IMPRINT",FACE,{"disambiguationData":[TD([[makeQuery(id+"F4.imprint","IMPRINT",EDGE,{"derivedFrom":subQ0}),1.0]])]});}
            var Q21;
            {var subQ0=sQuery(id+"F4.wireOp",EDGE,"E38.13.0");Q21=makeQuery(id+"F4.imprint","IMPRINT",FACE,{"disambiguationData":[TD([[makeQuery(id+"F4.imprint","IMPRINT",EDGE,{"derivedFrom":subQ0}),1.0]])]});}
            var Q22;
            {var subQ0=sQuery(id+"F4.wireOp",EDGE,"E38.11.0");Q22=makeQuery(id+"F4.imprint","IMPRINT",FACE,{"disambiguationData":[TD([[makeQuery(id+"F4.imprint","IMPRINT",EDGE,{"derivedFrom":subQ0}),1.0]])]});}
            var Q23;
            {var subQ0=sQuery(id+"F4.wireOp",EDGE,"E38.10.0");Q23=makeQuery(id+"F4.imprint","IMPRINT",FACE,{"disambiguationData":[TD([[makeQuery(id+"F4.imprint","IMPRINT",EDGE,{"derivedFrom":subQ0}),1.0]])]});}
            var Q24;
            {var subQ0=sQuery(id+"F4.wireOp",EDGE,"E38.9.0");Q24=makeQuery(id+"F4.imprint","IMPRINT",FACE,{"disambiguationData":[TD([[makeQuery(id+"F4.imprint","IMPRINT",EDGE,{"derivedFrom":subQ0}),1.0]])]});}
            var Q25;
            {var subQ0=sQuery(id+"F4.wireOp",EDGE,"E38.8.0");Q25=makeQuery(id+"F4.imprint","IMPRINT",FACE,{"disambiguationData":[TD([[makeQuery(id+"F4.imprint","IMPRINT",EDGE,{"derivedFrom":subQ0}),1.0]])]});}
            var Q26;
            {var subQ0=sQuery(id+"F4.wireOp",EDGE,"E38.7.0");Q26=makeQuery(id+"F4.imprint","IMPRINT",FACE,{"disambiguationData":[TD([[makeQuery(id+"F4.imprint","IMPRINT",EDGE,{"derivedFrom":subQ0}),1.0]])]});}
            var Q27;
            {var subQ0=sQuery(id+"F4.wireOp",EDGE,"E38.6.0");Q27=makeQuery(id+"F4.imprint","IMPRINT",FACE,{"disambiguationData":[TD([[makeQuery(id+"F4.imprint","IMPRINT",EDGE,{"derivedFrom":subQ0}),1.0]])]});}
            var Q28;
            {var subQ0=sQuery(id+"F4.wireOp",EDGE,"E38.5.0");Q28=makeQuery(id+"F4.imprint","IMPRINT",FACE,{"disambiguationData":[TD([[makeQuery(id+"F4.imprint","IMPRINT",EDGE,{"derivedFrom":subQ0}),1.0]])]});}
            var Q29;
            {var subQ0=sQuery(id+"F4.wireOp",EDGE,"E38.4.0");Q29=makeQuery(id+"F4.imprint","IMPRINT",FACE,{"disambiguationData":[TD([[makeQuery(id+"F4.imprint","IMPRINT",EDGE,{"derivedFrom":subQ0}),1.0]])]});}
            var Q30;
            {var subQ0=sQuery(id+"F4.wireOp",EDGE,"E38.3.0");Q30=makeQuery(id+"F4.imprint","IMPRINT",FACE,{"disambiguationData":[TD([[makeQuery(id+"F4.imprint","IMPRINT",EDGE,{"derivedFrom":subQ0}),1.0]])]});}
            var Q31;
            {var subQ0=sQuery(id+"F4.wireOp",EDGE,"E38.2.0");Q31=makeQuery(id+"F4.imprint","IMPRINT",FACE,{"disambiguationData":[TD([[makeQuery(id+"F4.imprint","IMPRINT",EDGE,{"derivedFrom":subQ0}),1.0]])]});}
            var Q32;
            {var subQ0=sQuery(id+"F4.wireOp",EDGE,"E38.1.0");Q32=makeQuery(id+"F4.imprint","IMPRINT",FACE,{"disambiguationData":[TD([[makeQuery(id+"F4.imprint","IMPRINT",EDGE,{"derivedFrom":subQ0}),1.0]])]});}
            var Q33;
            {var subQ0=sQuery(id+"F4.wireOp",EDGE,"E38.12.0");Q33=makeQuery(id+"F4.imprint","IMPRINT",FACE,{"disambiguationData":[TD([[makeQuery(id+"F4.imprint","IMPRINT",EDGE,{"derivedFrom":subQ0}),1.0]])]});}
            var Q34;
            Q34=makeQuery(id+"F1.opRevolve","SWEPT_FACE",FACE,{"disambiguationData":[OSD([sQuery(id+"F0.wireOp",EDGE,"E7")])]});
            extrude(context, id + "F5", {"entities" : qUnion([Q0, Q1, Q2, Q3, Q4, Q5, Q6, Q7, Q8, Q9, Q10, Q11, Q12, Q13, Q14, Q15, Q16, Q17, Q18, Q19, Q20, Q21, Q22, Q23, Q24, Q25, Q26, Q27, Q28, Q29, Q30, Q31, Q32, Q33]), "operationType" : NewBodyOperationType.REMOVE, "endBound" : BoundingType.UP_TO_SURFACE, "oppositeDirection" : true, "endBoundEntityFace" : qUnion([Q34]), "depth" : 59.05 * mm});
        }
    });
